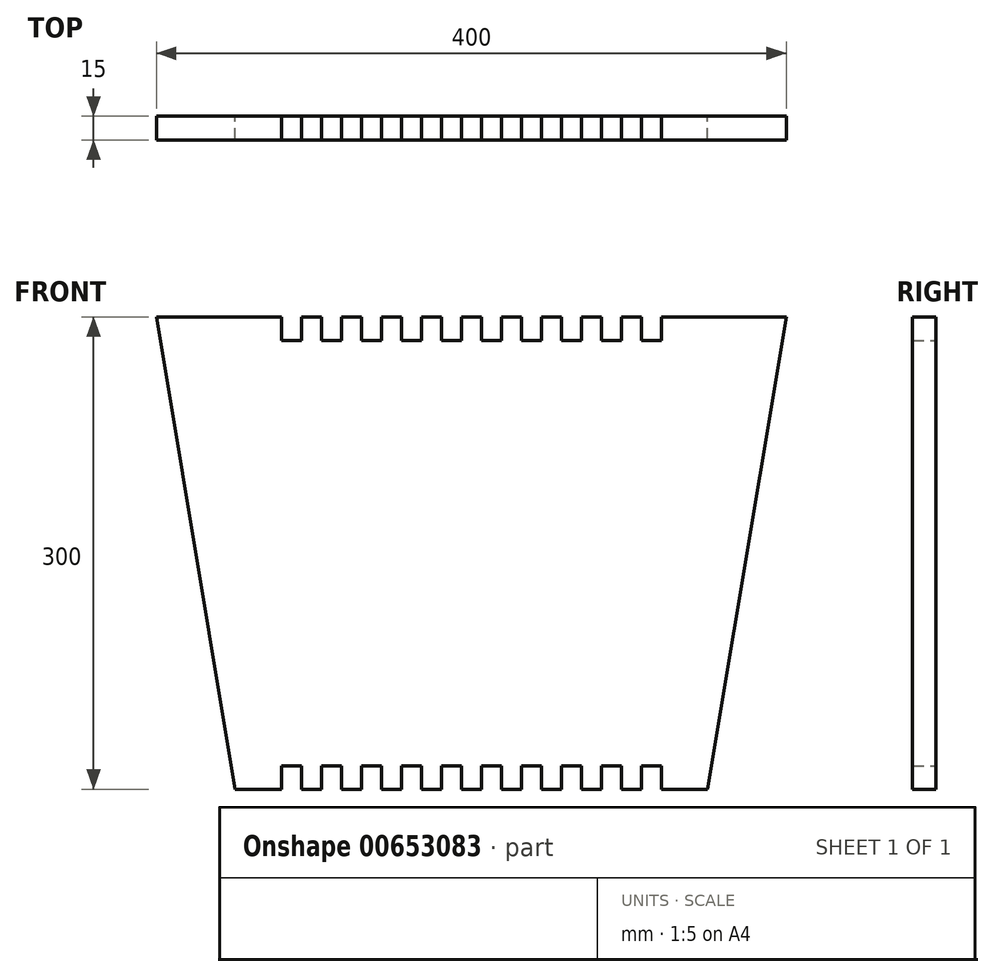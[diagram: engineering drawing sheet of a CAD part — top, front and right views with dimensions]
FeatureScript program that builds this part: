
annotation { "Feature Type Name" : "Feature", "Feature Type Description" : "" }
export const myFeature = defineFeature(function(context is Context, id is Id, definition is map)
    precondition{}
    {
        {
            var Q0;
            Q0=qCreatedBy(makeId("Front.planeOp"),FACE);
            var sketch = newSketch(context, id + "F0", { "sketchPlane" : qUnion([Q0])});
            skLineSegment(sketch, "E0.top", {"start": v(200, 150) * mm, "end": v(-200, 150) * mm});
            skPoint(sketch, "E0.middle", {"position": v(0, 0) * mm});
            skLineSegment(sketch, "E1.bottom", {"start": v(150, -150) * mm, "end": v(-150, -150) * mm});
            skLineSegment(sketch, "E2", {"start": v(-200, 150) * mm, "end": v(-150, -150) * mm});
            skLineSegment(sketch, "E3", {"start": v(150, -150) * mm, "end": v(200, 150) * mm});
            skLineSegment(sketch, "E4", {"start": v(0, 150) * mm, "end": v(-6.35, 150) * mm});
            skLineSegment(sketch, "E5.bottom", {"start": v(-6.35, 150) * mm, "end": v(-19.05, 150) * mm});
            skLineSegment(sketch, "E5.top", {"start": v(-6.35, 135) * mm, "end": v(-19.05, 135) * mm});
            skLineSegment(sketch, "E5.left", {"start": v(-6.35, 150) * mm, "end": v(-6.35, 135) * mm});
            skLineSegment(sketch, "E5.right", {"start": v(-19.05, 150) * mm, "end": v(-19.05, 135) * mm});
            skLineSegment(sketch, "E6.1.0.0", {"start": v(-44.45, 150) * mm, "end": v(-44.45, 135) * mm});
            skLineSegment(sketch, "E6.1.0.1", {"start": v(-31.75, 150) * mm, "end": v(-44.45, 150) * mm});
            skLineSegment(sketch, "E6.1.0.2", {"start": v(-31.75, 135) * mm, "end": v(-44.45, 135) * mm});
            skLineSegment(sketch, "E6.1.0.3", {"start": v(-31.75, 150) * mm, "end": v(-31.75, 135) * mm});
            skLineSegment(sketch, "E6.2.0.0", {"start": v(-69.85, 150) * mm, "end": v(-69.85, 135) * mm});
            skLineSegment(sketch, "E6.2.0.1", {"start": v(-57.15, 150) * mm, "end": v(-69.85, 150) * mm});
            skLineSegment(sketch, "E6.2.0.2", {"start": v(-57.15, 135) * mm, "end": v(-69.85, 135) * mm});
            skLineSegment(sketch, "E6.2.0.3", {"start": v(-57.15, 150) * mm, "end": v(-57.15, 135) * mm});
            skLineSegment(sketch, "E6.3.0.0", {"start": v(-95.25, 150) * mm, "end": v(-95.25, 135) * mm});
            skLineSegment(sketch, "E6.3.0.1", {"start": v(-82.55, 150) * mm, "end": v(-95.25, 150) * mm});
            skLineSegment(sketch, "E6.3.0.2", {"start": v(-82.55, 135) * mm, "end": v(-95.25, 135) * mm});
            skLineSegment(sketch, "E6.3.0.3", {"start": v(-82.55, 150) * mm, "end": v(-82.55, 135) * mm});
            skLineSegment(sketch, "E6.4.0.0", {"start": v(-120.65, 150) * mm, "end": v(-120.65, 135) * mm});
            skLineSegment(sketch, "E6.4.0.1", {"start": v(-107.95, 150) * mm, "end": v(-120.65, 150) * mm});
            skLineSegment(sketch, "E6.4.0.2", {"start": v(-107.95, 135) * mm, "end": v(-120.65, 135) * mm});
            skLineSegment(sketch, "E6.4.0.3", {"start": v(-107.95, 150) * mm, "end": v(-107.95, 135) * mm});
            skLineSegment(sketch, "E6.direction1", {"start": v(-19.05, 135) * mm, "end": v(-44.45, 135) * mm, "construction": true});
            skLineSegment(sketch, "E7.1.0.0", {"start": v(6.35, 150) * mm, "end": v(6.35, 135) * mm});
            skLineSegment(sketch, "E7.1.0.1", {"start": v(19.05, 150) * mm, "end": v(6.35, 150) * mm});
            skLineSegment(sketch, "E7.1.0.2", {"start": v(19.05, 150) * mm, "end": v(19.05, 135) * mm});
            skLineSegment(sketch, "E7.1.0.3", {"start": v(19.05, 135) * mm, "end": v(6.35, 135) * mm});
            skLineSegment(sketch, "E7.2.0.0", {"start": v(31.75, 150) * mm, "end": v(31.75, 135) * mm});
            skLineSegment(sketch, "E7.2.0.1", {"start": v(44.45, 150) * mm, "end": v(31.75, 150) * mm});
            skLineSegment(sketch, "E7.2.0.2", {"start": v(44.45, 150) * mm, "end": v(44.45, 135) * mm});
            skLineSegment(sketch, "E7.2.0.3", {"start": v(44.45, 135) * mm, "end": v(31.75, 135) * mm});
            skLineSegment(sketch, "E7.3.0.0", {"start": v(57.15, 150) * mm, "end": v(57.15, 135) * mm});
            skLineSegment(sketch, "E7.3.0.1", {"start": v(69.85, 150) * mm, "end": v(57.15, 150) * mm});
            skLineSegment(sketch, "E7.3.0.2", {"start": v(69.85, 150) * mm, "end": v(69.85, 135) * mm});
            skLineSegment(sketch, "E7.3.0.3", {"start": v(69.85, 135) * mm, "end": v(57.15, 135) * mm});
            skLineSegment(sketch, "E7.4.0.0", {"start": v(82.55, 150) * mm, "end": v(82.55, 135) * mm});
            skLineSegment(sketch, "E7.4.0.1", {"start": v(95.25, 150) * mm, "end": v(82.55, 150) * mm});
            skLineSegment(sketch, "E7.4.0.2", {"start": v(95.25, 150) * mm, "end": v(95.25, 135) * mm});
            skLineSegment(sketch, "E7.4.0.3", {"start": v(95.25, 135) * mm, "end": v(82.55, 135) * mm});
            skLineSegment(sketch, "E7.5.0.0", {"start": v(107.95, 150) * mm, "end": v(107.95, 135) * mm});
            skLineSegment(sketch, "E7.5.0.1", {"start": v(120.65, 150) * mm, "end": v(107.95, 150) * mm});
            skLineSegment(sketch, "E7.5.0.2", {"start": v(120.65, 150) * mm, "end": v(120.65, 135) * mm});
            skLineSegment(sketch, "E7.5.0.3", {"start": v(120.65, 135) * mm, "end": v(107.95, 135) * mm});
            skLineSegment(sketch, "E7.direction1", {"start": v(-19.05, 135) * mm, "end": v(6.35, 135) * mm, "construction": true});
            skLineSegment(sketch, "E8", {"start": v(0, 150) * mm, "end": v(0, -150) * mm, "construction": true});
            skLineSegment(sketch, "E9.MirrorCS", {"start": v(0, -150) * mm, "end": v(-6.35, -150) * mm});
            skLineSegment(sketch, "E10.MirrorCS", {"start": v(69.85, -150) * mm, "end": v(57.15, -150) * mm});
            skLineSegment(sketch, "E11.MirrorCS", {"start": v(-69.85, -150) * mm, "end": v(-69.85, -135) * mm});
            skLineSegment(sketch, "E12.MirrorCS", {"start": v(-57.15, -150) * mm, "end": v(-69.85, -150) * mm});
            skLineSegment(sketch, "E13.MirrorCS", {"start": v(-82.55, -150) * mm, "end": v(-82.55, -135) * mm});
            skLineSegment(sketch, "E14.MirrorCS", {"start": v(-19.05, -150) * mm, "end": v(-19.05, -135) * mm});
            skLineSegment(sketch, "E15.MirrorCS", {"start": v(-31.75, -150) * mm, "end": v(-31.75, -135) * mm});
            skLineSegment(sketch, "E16.MirrorCS", {"start": v(-95.25, -150) * mm, "end": v(-95.25, -135) * mm});
            skLineSegment(sketch, "E17.MirrorCS", {"start": v(120.65, -135) * mm, "end": v(107.95, -135) * mm});
            skLineSegment(sketch, "E18.MirrorCS", {"start": v(69.85, -150) * mm, "end": v(69.85, -135) * mm});
            skLineSegment(sketch, "E19.MirrorCS", {"start": v(-57.15, -150) * mm, "end": v(-57.15, -135) * mm});
            skLineSegment(sketch, "E20.MirrorCS", {"start": v(44.45, -150) * mm, "end": v(44.45, -135) * mm});
            skLineSegment(sketch, "E21.MirrorCS", {"start": v(95.25, -135) * mm, "end": v(82.55, -135) * mm});
            skLineSegment(sketch, "E22.MirrorCS", {"start": v(82.55, -150) * mm, "end": v(82.55, -135) * mm});
            skLineSegment(sketch, "E23.MirrorCS", {"start": v(44.45, -150) * mm, "end": v(31.75, -150) * mm});
            skLineSegment(sketch, "E24.MirrorCS", {"start": v(-82.55, -150) * mm, "end": v(-95.25, -150) * mm});
            skLineSegment(sketch, "E25.MirrorCS", {"start": v(120.65, -150) * mm, "end": v(120.65, -135) * mm});
            skLineSegment(sketch, "E26.MirrorCS", {"start": v(19.05, -150) * mm, "end": v(19.05, -135) * mm});
            skLineSegment(sketch, "E27.MirrorCS", {"start": v(95.25, -150) * mm, "end": v(95.25, -135) * mm});
            skLineSegment(sketch, "E28.MirrorCS", {"start": v(-107.95, -150) * mm, "end": v(-107.95, -135) * mm});
            skLineSegment(sketch, "E29.MirrorCS", {"start": v(-120.65, -150) * mm, "end": v(-120.65, -135) * mm});
            skLineSegment(sketch, "E30.MirrorCS", {"start": v(-19.05, -135) * mm, "end": v(6.35, -135) * mm, "construction": true});
            skLineSegment(sketch, "E31.MirrorCS", {"start": v(69.85, -135) * mm, "end": v(57.15, -135) * mm});
            skLineSegment(sketch, "E32.MirrorCS", {"start": v(44.45, -135) * mm, "end": v(31.75, -135) * mm});
            skLineSegment(sketch, "E33.MirrorCS", {"start": v(57.15, -150) * mm, "end": v(57.15, -135) * mm});
            skLineSegment(sketch, "E34.MirrorCS", {"start": v(-31.75, -135) * mm, "end": v(-44.45, -135) * mm});
            skLineSegment(sketch, "E35.MirrorCS", {"start": v(-31.75, -150) * mm, "end": v(-44.45, -150) * mm});
            skLineSegment(sketch, "E36.MirrorCS", {"start": v(-6.35, -150) * mm, "end": v(-6.35, -135) * mm});
            skLineSegment(sketch, "E37.MirrorCS", {"start": v(19.05, -135) * mm, "end": v(6.35, -135) * mm});
            skLineSegment(sketch, "E38.MirrorCS", {"start": v(120.65, -150) * mm, "end": v(107.95, -150) * mm});
            skLineSegment(sketch, "E39.MirrorCS", {"start": v(-44.45, -150) * mm, "end": v(-44.45, -135) * mm});
            skLineSegment(sketch, "E40.MirrorCS", {"start": v(6.35, -150) * mm, "end": v(6.35, -135) * mm});
            skLineSegment(sketch, "E41.MirrorCS", {"start": v(-6.35, -150) * mm, "end": v(-19.05, -150) * mm});
            skLineSegment(sketch, "E42.MirrorCS", {"start": v(-6.35, -135) * mm, "end": v(-19.05, -135) * mm});
            skLineSegment(sketch, "E43.MirrorCS", {"start": v(-82.55, -135) * mm, "end": v(-95.25, -135) * mm});
            skLineSegment(sketch, "E44.MirrorCS", {"start": v(31.75, -150) * mm, "end": v(31.75, -135) * mm});
            skLineSegment(sketch, "E45.MirrorCS", {"start": v(95.25, -150) * mm, "end": v(82.55, -150) * mm});
            skLineSegment(sketch, "E46.MirrorCS", {"start": v(19.05, -150) * mm, "end": v(6.35, -150) * mm});
            skLineSegment(sketch, "E47.MirrorCS", {"start": v(-57.15, -135) * mm, "end": v(-69.85, -135) * mm});
            skLineSegment(sketch, "E48.MirrorCS", {"start": v(-107.95, -135) * mm, "end": v(-120.65, -135) * mm});
            skLineSegment(sketch, "E49.MirrorCS", {"start": v(107.95, -150) * mm, "end": v(107.95, -135) * mm});
            skLineSegment(sketch, "E50.MirrorCS", {"start": v(-107.95, -150) * mm, "end": v(-120.65, -150) * mm});
            skLineSegment(sketch, "E51.MirrorCS", {"start": v(-19.05, -135) * mm, "end": v(-44.45, -135) * mm, "construction": true});
            skSolve(sketch);
        }
        {
            var Q0;
            {var subQ11=sQuery(id+"F0.wireOp",EDGE,"E4");Q0=makeQuery(id+"F0.imprint","IMPRINT",FACE,{"disambiguationData":[TD([[makeQuery(id+"F0.imprint","IMPRINT",EDGE,{"derivedFrom":subQ11}),1.0]])]});}
            var Q1;
            {var subQ20=sQuery(id+"F0.wireOp",EDGE,"5a77793a-1603-48c1-be9b-ca43dec4514b0.MirrorCS");Q1=makeQuery(id+"F0.imprint","IMPRINT",FACE,{"disambiguationData":[TD([[makeQuery(id+"F0.imprint","IMPRINT",EDGE,{"derivedFrom":subQ20}),-1.0]])]});}
            var Q2;
            {var subQ19=sQuery(id+"F0.wireOp",EDGE,"E7.1.0.0");Q2=makeQuery(id+"F0.imprint","IMPRINT",FACE,{"disambiguationData":[TD([[makeQuery(id+"F0.imprint","IMPRINT",EDGE,{"derivedFrom":subQ19}),-1.0]])]});}
            var Q3;
            Q3=makeQuery(id+"F0.imprint","IMPRINT",FACE,{"disambiguationData":[TD([[makeQuery(id+"F0.imprint","IMPRINT",EDGE,{"derivedFrom":sQuery(id+"F0.wireOp",EDGE,"5a77793a-1603-48c1-be9b-ca43dec4514b4.MirrorCS")}),-1.0]])]});
            extrude(context, id + "F1", {"entities" : qUnion([Q0, Q1, Q2, Q3]), "depth" : 15 * mm, "offsetDistance" : 25 * mm});
        }
    });
